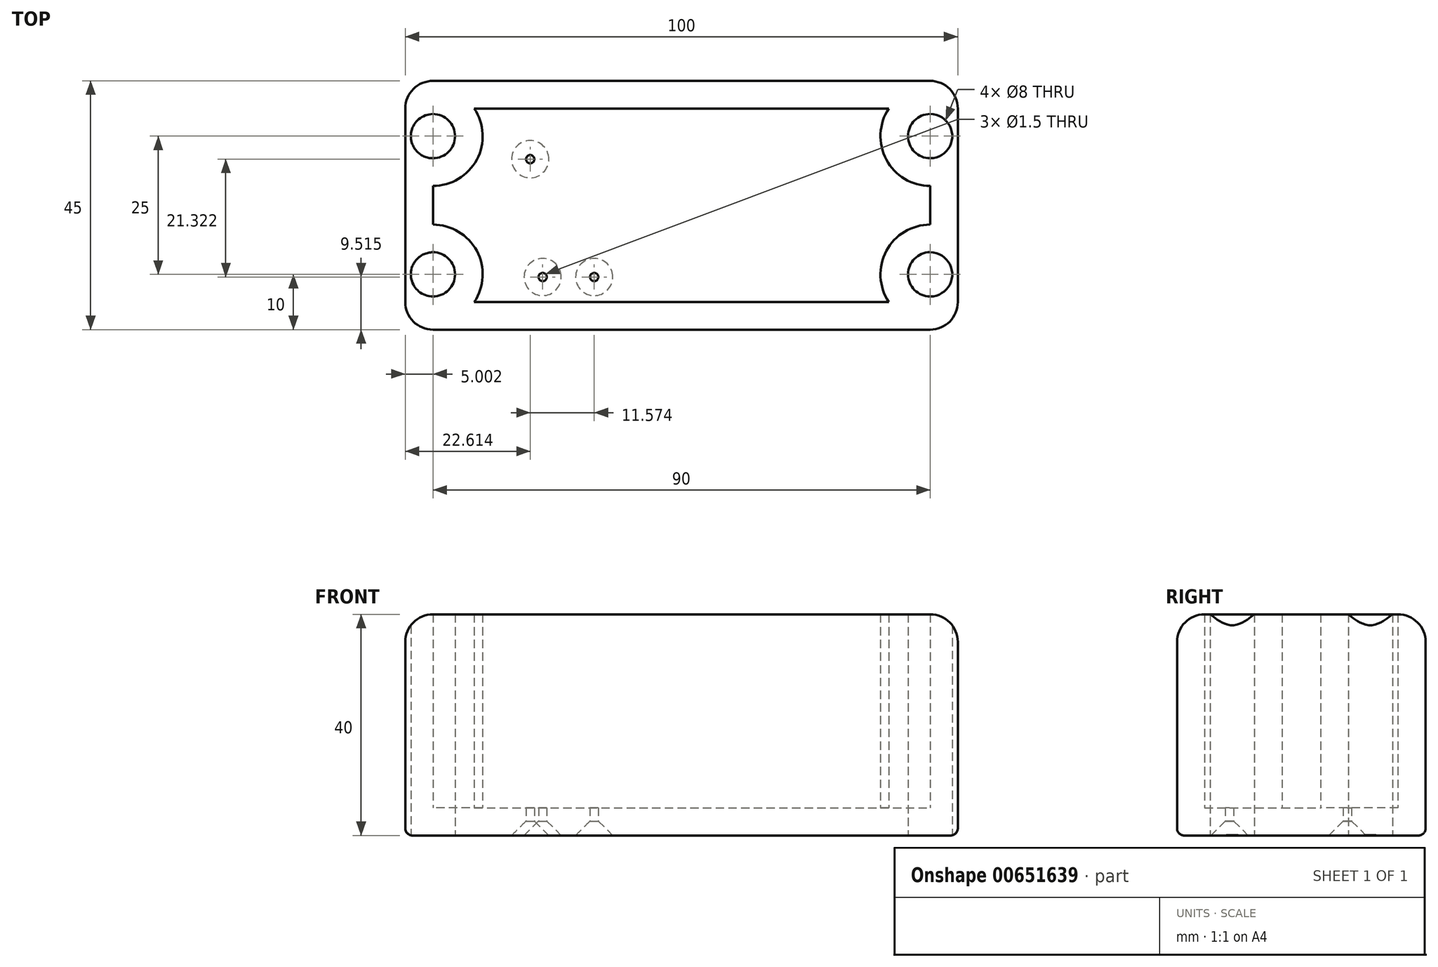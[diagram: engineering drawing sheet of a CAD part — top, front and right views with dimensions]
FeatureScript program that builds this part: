
annotation { "Feature Type Name" : "Feature", "Feature Type Description" : "" }
export const myFeature = defineFeature(function(context is Context, id is Id, definition is map)
    precondition{}
    {
        {
            var Q0;
            Q0=qCreatedBy(makeId("Top.planeOp"),FACE);
            var sketch = newSketch(context, id + "F0", { "sketchPlane" : qUnion([Q0])});
            skLineSegment(sketch, "E0.bottom", {"start": v(-60.6, 0) * mm, "end": v(39.4, 0) * mm});
            skLineSegment(sketch, "E0.top", {"start": v(-60.6, 45) * mm, "end": v(39.4, 45) * mm});
            skLineSegment(sketch, "E0.left", {"start": v(-60.6, 0) * mm, "end": v(-60.6, 45) * mm});
            skLineSegment(sketch, "E0.right", {"start": v(39.4, 0) * mm, "end": v(39.4, 45) * mm});
            skCircle(sketch, "E1", {"center": v(-55.6, 35) * mm, "radius": 4 * mm});
            skLineSegment(sketch, "E2", {"start": v(-60.6, 22.5) * mm, "end": v(39.4, 22.5) * mm, "construction": true});
            skLineSegment(sketch, "E3", {"start": v(-10.6, 45) * mm, "end": v(-10.6, 0) * mm, "construction": true});
            skCircle(sketch, "E4.MirrorC", {"center": v(-55.6, 10) * mm, "radius": 4 * mm});
            skCircle(sketch, "E5.MirrorC", {"center": v(34.4, 35) * mm, "radius": 4 * mm});
            skCircle(sketch, "E6.MirrorC", {"center": v(34.4, 10) * mm, "radius": 4 * mm});
            skPoint(sketch, "E7", {"position": v(-35.75, 9.52) * mm});
            skPoint(sketch, "E8", {"position": v(-26.42, 9.52) * mm});
            skPoint(sketch, "E9", {"position": v(-38, 30.84) * mm});
            skSolve(sketch);
        }
        {
            var Q0;
            Q0=makeQuery(id+"F0.imprint","IMPRINT",FACE,{"disambiguationData":[TD([[makeQuery(id+"F0.imprint","IMPRINT",EDGE,{"derivedFrom":sQuery(id+"F0.wireOp",EDGE,"E0.bottom")}),1.0]])]});
            extrude(context, id + "F1", {"entities" : qUnion([Q0]), "depth" : 40 * mm, "offsetDistance" : 25 * mm});
        }
        {
            var Q0;
            Q0=makeQuery(id+"F1.opExtrude","CAP_FACE",FACE,{"disambiguationData":[OSD([sQuery(id+"F0.wireOp",EDGE,"E0.bottom"),sQuery(id+"F0.wireOp",EDGE,"E0.top"),sQuery(id+"F0.wireOp",EDGE,"E0.left"),sQuery(id+"F0.wireOp",EDGE,"E0.right"),sQuery(id+"F0.wireOp",EDGE,"E1"),sQuery(id+"F0.wireOp",EDGE,"E4.MirrorC"),sQuery(id+"F0.wireOp",EDGE,"E5.MirrorC"),sQuery(id+"F0.wireOp",EDGE,"E6.MirrorC")])],"isStart":false});
            shell(context, id + "F2", {"entities" : qUnion([Q0]), "thickness" : 5 * mm});
        }
        {
            var Q0;
            Q0=makeQuery(id+"F1.opExtrude","CAP_EDGE",EDGE,{"disambiguationData":[OSD([sQuery(id+"F0.wireOp",EDGE,"E0.bottom")])],"isStart":true});
            var Q1;
            Q1=makeQuery(id+"F1.opExtrude","CAP_EDGE",EDGE,{"disambiguationData":[OSD([sQuery(id+"F0.wireOp",EDGE,"E0.right")])],"isStart":true});
            var Q2;
            Q2=makeQuery(id+"F1.opExtrude","CAP_EDGE",EDGE,{"disambiguationData":[OSD([sQuery(id+"F0.wireOp",EDGE,"E0.top")])],"isStart":true});
            var Q3;
            Q3=makeQuery(id+"F1.opExtrude","CAP_EDGE",EDGE,{"disambiguationData":[OSD([sQuery(id+"F0.wireOp",EDGE,"E0.left")])],"isStart":true});
            fillet(context, id + "F3", {"entities" : qUnion([Q0, Q1, Q2, Q3]), "radius" : 1.3 * mm, "tangentPropagation" : true, "allowEdgeOverflow" : false});
        }
        {
            var Q0;
            Q0=sQuery(id+"F0.wireOp",VERTEX,"E7");
            var Q1;
            Q1=sQuery(id+"F0.wireOp",VERTEX,"E9");
            var Q2;
            Q2=sQuery(id+"F0.wireOp",VERTEX,"E8");
            var Q3;
            Q3=makeQuery(id+"F1.opExtrude","SWEPT_BODY",BODY,{"disambiguationData":[OSD([sQuery(id+"F0.wireOp",EDGE,"E0.bottom"),sQuery(id+"F0.wireOp",EDGE,"E0.top"),sQuery(id+"F0.wireOp",EDGE,"E0.left"),sQuery(id+"F0.wireOp",EDGE,"E0.right"),sQuery(id+"F0.wireOp",EDGE,"E1"),sQuery(id+"F0.wireOp",EDGE,"E4.MirrorC"),sQuery(id+"F0.wireOp",EDGE,"E5.MirrorC"),sQuery(id+"F0.wireOp",EDGE,"E6.MirrorC")])]});
            hole(context, id + "F4", {"style" : HoleStyle.C_SINK, "endStyle" : HoleEndStyle.BLIND, "oppositeDirection" : true, "standardTappedOrClearance" : lookupTablePath({ "standard" : "ISO", "size" : "1.5", "type" : "Drilled" }), "standardBlindInLast" : lookupTablePath({ "standard" : "ISO", "size" : "1.5", "type" : "Drilled" }), "holeDiameter" : 1.5 * mm, "cSinkDiameter" : 6.72 * mm, "cSinkAngle" : 90 * degree, "majorDiameter" : 3 * mm, "holeDepth" : 11.5 * mm, "tappedDepth" : 10 * mm, "tapClearance" : 3, "locations" : qUnion([Q0, Q1, Q2]), "scope" : qUnion([Q3])});
        }
        {
            var Q0;
            Q0=makeQuery(id+"F1.opExtrude","SWEPT_BODY",BODY,{"disambiguationData":[OSD([sQuery(id+"F0.wireOp",EDGE,"E0.bottom"),sQuery(id+"F0.wireOp",EDGE,"E0.top"),sQuery(id+"F0.wireOp",EDGE,"E0.left"),sQuery(id+"F0.wireOp",EDGE,"E0.right"),sQuery(id+"F0.wireOp",EDGE,"E1"),sQuery(id+"F0.wireOp",EDGE,"E4.MirrorC"),sQuery(id+"F0.wireOp",EDGE,"E5.MirrorC"),sQuery(id+"F0.wireOp",EDGE,"E6.MirrorC")])]});
            transform(context, id + "F5", {"entities" : qUnion([Q0]), "transformType" : TransformType.TRANSLATION_3D, "dx" : 0 * mm, "dy" : 0 * mm, "dz" : 0 * mm, "makeCopy" : false});
        }
        {
            var Q0;
            Q0=makeQuery(id+"F1.opExtrude","CAP_EDGE",EDGE,{"disambiguationData":[OSD([sQuery(id+"F0.wireOp",EDGE,"E0.bottom")])],"isStart":false});
            fillet(context, id + "F6", {"entities" : qUnion([Q0]), "radius" : 5 * mm, "tangentPropagation" : true, "allowEdgeOverflow" : false});
        }
        {
            var Q0;
            Q0=makeQuery(id+"F1.opExtrude","CAP_EDGE",EDGE,{"disambiguationData":[OSD([sQuery(id+"F0.wireOp",EDGE,"E0.top")])],"isStart":false});
            fillet(context, id + "F7", {"entities" : qUnion([Q0]), "radius" : 5 * mm, "tangentPropagation" : true, "allowEdgeOverflow" : false});
        }
        {
            var Q0;
            Q0=makeQuery(id+"F1.opExtrude","CAP_EDGE",EDGE,{"disambiguationData":[OSD([sQuery(id+"F0.wireOp",EDGE,"E0.right")])],"isStart":false});
            var Q1;
            Q1=makeQuery(id+"F1.opExtrude","CAP_EDGE",EDGE,{"disambiguationData":[OSD([sQuery(id+"F0.wireOp",EDGE,"E0.left")])],"isStart":false});
            fillet(context, id + "F8", {"entities" : qUnion([Q0, Q1]), "radius" : 5 * mm, "tangentPropagation" : true, "allowEdgeOverflow" : false});
        }
    });
